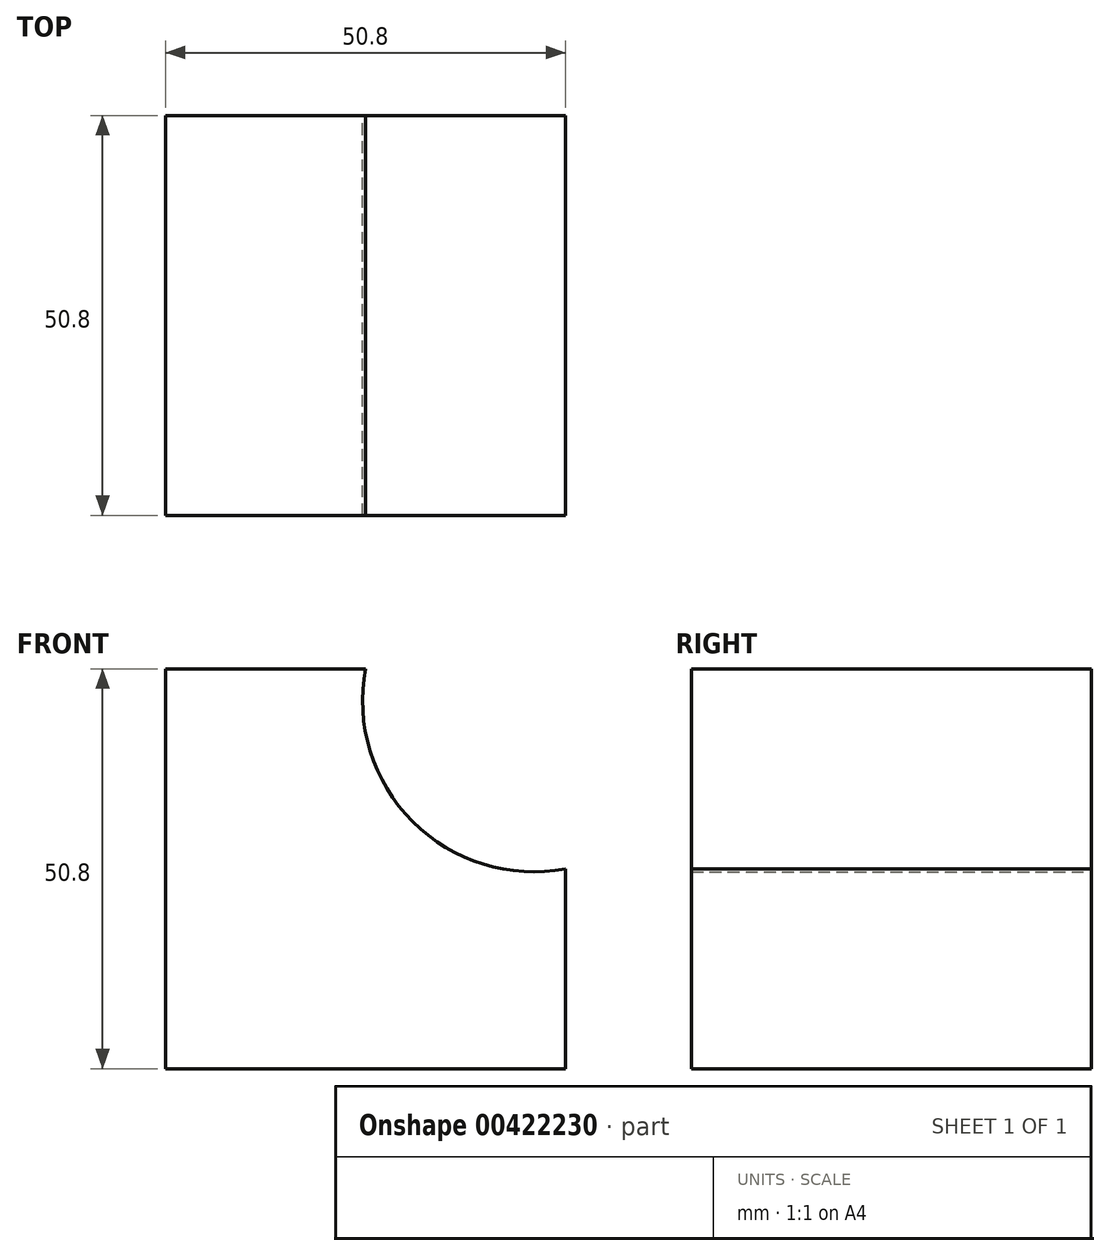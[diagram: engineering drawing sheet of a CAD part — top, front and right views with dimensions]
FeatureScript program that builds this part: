
annotation { "Feature Type Name" : "Feature", "Feature Type Description" : "" }
export const myFeature = defineFeature(function(context is Context, id is Id, definition is map)
    precondition{}
    {
        {
            var Q0;
            Q0=qCreatedBy(makeId("Front.planeOp"),FACE);
            var sketch = newSketch(context, id + "F0", { "sketchPlane" : qUnion([Q0])});
            skLineSegment(sketch, "E0", {"start": v(-24.7, 59.7) * mm, "end": v(-24.7, 8.9) * mm});
            skLineSegment(sketch, "E1", {"start": v(-24.7, 59.7) * mm, "end": v(0.7, 59.7) * mm});
            skLineSegment(sketch, "E2", {"start": v(-24.7, 8.9) * mm, "end": v(26.1, 8.9) * mm});
            skLineSegment(sketch, "E3", {"start": v(26.1, 8.9) * mm, "end": v(26.1, 34.3) * mm});
            skArc(sketch, "E4", {"start": v(0.7, 59.7) * mm, "mid": v(6.7, 40.28) * mm, "end": v(26.1, 34.3) * mm});
            skSolve(sketch);
        }
        {
            var Q0;
            Q0 = qSketchRegion(id + "F0", true);
            extrude(context, id + "F1", {"entities" : qUnion([Q0]), "depth" : 50.8 * mm});
        }
    });
